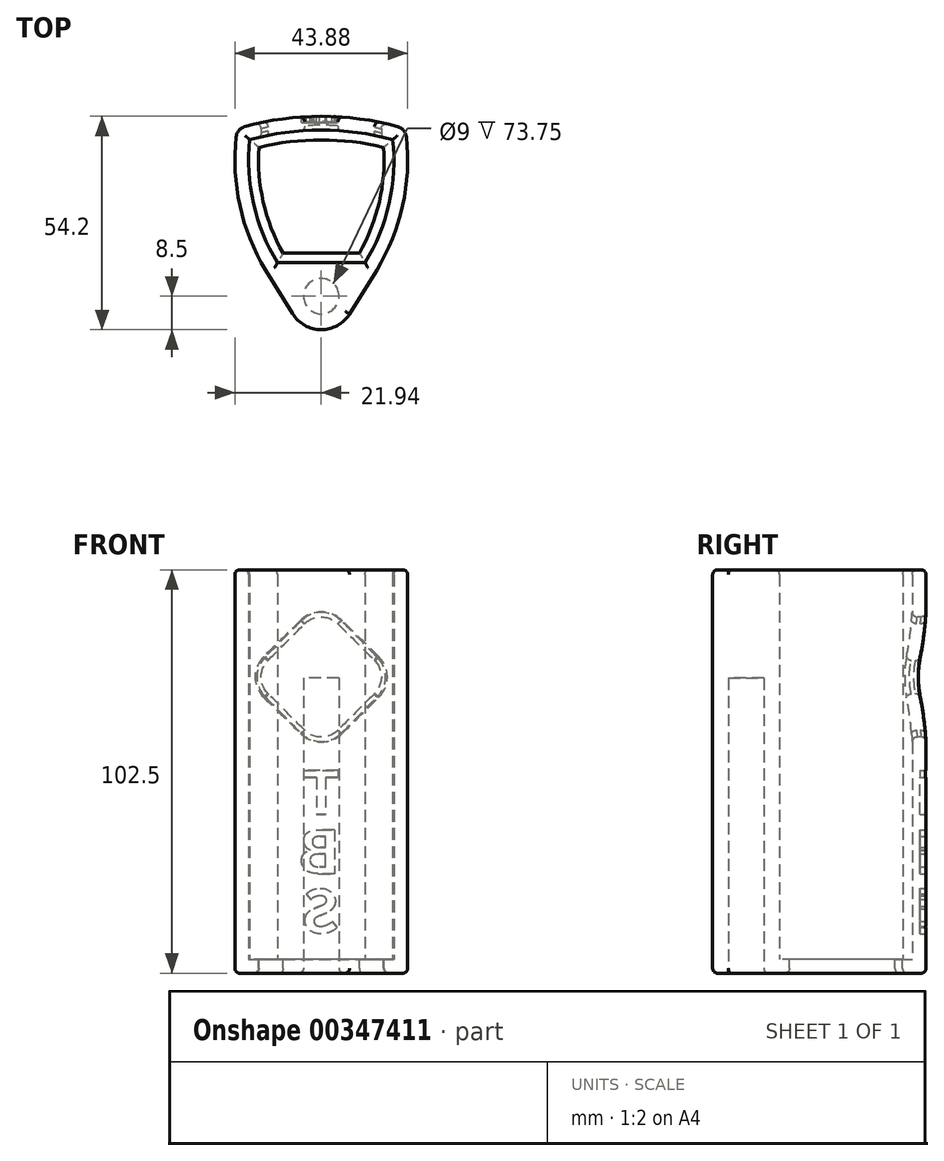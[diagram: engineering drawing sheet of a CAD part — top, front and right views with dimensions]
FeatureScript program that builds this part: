
annotation { "Feature Type Name" : "Feature", "Feature Type Description" : "" }
export const myFeature = defineFeature(function(context is Context, id is Id, definition is map)
    precondition{}
    {
        {
            var Q0;
            Q0=qCreatedBy(makeId("Top.planeOp"),FACE);
            var sketch = newSketch(context, id + "F0", { "sketchPlane" : qUnion([Q0])});
            skLineSegment(sketch, "E0", {"start": v(0, 0) * mm, "end": v(11.12, 0) * mm});
            skLineSegment(sketch, "E1", {"start": v(11.12, 0) * mm, "end": v(-11.12, 0) * mm});
            skArc(sketch, "E2", {"start": v(-18.16, 31.28) * mm, "mid": v(-17.22, 15.06) * mm, "end": v(-11.13, 0) * mm});
            skArc(sketch, "E3", {"start": v(11.13, 0) * mm, "mid": v(17.22, 15.06) * mm, "end": v(18.16, 31.28) * mm});
            skArc(sketch, "E4", {"start": v(18.16, 31.28) * mm, "mid": v(0, 33.7) * mm, "end": v(-18.16, 31.28) * mm});
            skArc(sketch, "E5.0", {"start": v(-21.34, 34) * mm, "mid": v(-20.88, 15.46) * mm, "end": v(-14.11, -1.82) * mm});
            skArc(sketch, "E5.1", {"start": v(21.34, 34) * mm, "mid": v(0, 37.2) * mm, "end": v(-21.34, 34) * mm});
            skArc(sketch, "E5.2", {"start": v(14.11, -1.82) * mm, "mid": v(20.88, 15.46) * mm, "end": v(21.34, 34) * mm});
            skCircle(sketch, "E6", {"center": v(0, -8.5) * mm, "radius": 4.5 * mm});
            skLineSegment(sketch, "E7", {"start": v(-14.11, -1.82) * mm, "end": v(-7.23, -12.97) * mm});
            skLineSegment(sketch, "E8", {"start": v(7.19, -13.03) * mm, "end": v(14.11, -1.82) * mm});
            skArc(sketch, "E9", {"start": v(-7.23, -12.97) * mm, "mid": v(-0.04, -17) * mm, "end": v(7.19, -13.03) * mm});
            skLineSegment(sketch, "E10", {"start": v(21.34, 34) * mm, "end": v(21.34, 39.15) * mm});
            skLineSegment(sketch, "E11", {"start": v(21.34, 39.15) * mm, "end": v(-21.34, 39.15) * mm});
            skLineSegment(sketch, "E12", {"start": v(-21.34, 39.15) * mm, "end": v(-21.34, 34) * mm});
            skSolve(sketch);
        }
        {
            var Q0;
            {var subQ3=sQuery(id+"F0.wireOp",EDGE,"E2");Q0=makeQuery(id+"F0.imprint","IMPRINT",FACE,{"disambiguationData":[TD([[makeQuery(id+"F0.imprint","IMPRINT",EDGE,{"derivedFrom":subQ3}),-1.0]])]});}
            var Q1;
            Q1=makeQuery(id+"F0.imprint","IMPRINT",FACE,{"disambiguationData":[TD([[makeQuery(id+"F0.imprint","IMPRINT",EDGE,{"derivedFrom":sQuery(id+"F0.wireOp",EDGE,"E6")}),1.0]])]});
            extrude(context, id + "F1", {"entities" : qUnion([Q0, Q1]), "depth" : 102.5 * mm});
        }
        {
            var Q0;
            {var subQ1=sQuery(id+"F0.wireOp",EDGE,"E2");Q0=makeQuery(id+"F0.imprint","IMPRINT",FACE,{"disambiguationData":[TD([[makeQuery(id+"F0.imprint","IMPRINT",EDGE,{"derivedFrom":subQ1}),1.0]])]});}
            extrude(context, id + "F2", {"entities" : qUnion([Q0]), "operationType" : NewBodyOperationType.ADD, "depth" : 3.5 * mm});
        }
        {
            var Q0;
            Q0=makeQuery(id+"F0.imprint","IMPRINT",FACE,{"disambiguationData":[TD([[makeQuery(id+"F0.imprint","IMPRINT",EDGE,{"derivedFrom":sQuery(id+"F0.wireOp",EDGE,"E6")}),1.0]])]});
            extrude(context, id + "F3", {"entities" : qUnion([Q0]), "operationType" : NewBodyOperationType.REMOVE, "depth" : 75 * mm});
        }
        {
            var Q0;
            Q0=makeQuery(id+"F0.imprint","IMPRINT",FACE,{"disambiguationData":[TD([[makeQuery(id+"F0.imprint","IMPRINT",EDGE,{"derivedFrom":sQuery(id+"F0.wireOp",EDGE,"E5.1")}),-1.0]])]});
            extrude(context, id + "F4", {"entities" : qUnion([Q0]), "operationType" : NewBodyOperationType.ADD, "depth" : 102.5 * mm});
        }
        {
            var Q0;
            Q0=makeQuery(id+"F4.opExtrude","SWEPT_FACE",FACE,{"disambiguationData":[OSD([sQuery(id+"F0.wireOp",EDGE,"E11")])]});
            var sketch = newSketch(context, id + "F5", { "sketchPlane" : qUnion([Q0])});
            skPoint(sketch, "E13.endSnap0", {"position": v(0, 0) * mm});
            skLineSegment(sketch, "E14", {"start": v(-17.75, 75.25) * mm, "end": v(0, 93) * mm});
            skLineSegment(sketch, "E15", {"start": v(17.75, 75.25) * mm, "end": v(0, 57.5) * mm});
            skLineSegment(sketch, "E16", {"start": v(0, 57.5) * mm, "end": v(-17.75, 75.25) * mm});
            skLineSegment(sketch, "E17", {"start": v(0, 93) * mm, "end": v(17.75, 75.25) * mm});
            skLineSegment(sketch, "E18", {"start": v(0, 0) * mm, "end": v(0, 57.5) * mm});
            skSolve(sketch);
        }
        {
            var Q0;
            Q0=makeQuery(id+"F5.imprint","IMPRINT",FACE,{"disambiguationData":[TD([[makeQuery(id+"F5.imprint","IMPRINT",EDGE,{"derivedFrom":sQuery(id+"F5.wireOp",EDGE,"E14")}),-1.0]])]});
            extrude(context, id + "F6", {"entities" : qUnion([Q0]), "operationType" : NewBodyOperationType.REMOVE, "oppositeDirection" : true, "depth" : 10 * mm});
        }
        {
            var Q0;
            Q0=makeQuery(id+"F6.boolean.opBoolean","COPY",EDGE,{"derivedFrom":makeQuery(id+"F6.opExtrude","SWEPT_EDGE",EDGE,{"disambiguationData":[OSD([sQuery(id+"F5.wireOp",EDGE,"E15"),sQuery(id+"F5.wireOp",EDGE,"E17")])]})});
            var Q1;
            Q1=makeQuery(id+"F6.boolean.opBoolean","COPY",EDGE,{"derivedFrom":makeQuery(id+"F6.opExtrude","SWEPT_EDGE",EDGE,{"disambiguationData":[OSD([sQuery(id+"F5.wireOp",EDGE,"E15"),sQuery(id+"F5.wireOp",EDGE,"E16")])]})});
            var Q2;
            Q2=makeQuery(id+"F6.boolean.opBoolean","COPY",EDGE,{"derivedFrom":makeQuery(id+"F6.opExtrude","SWEPT_EDGE",EDGE,{"disambiguationData":[OSD([sQuery(id+"F5.wireOp",EDGE,"E14"),sQuery(id+"F5.wireOp",EDGE,"E16")])]})});
            var Q3;
            Q3=makeQuery(id+"F6.boolean.opBoolean","COPY",EDGE,{"derivedFrom":makeQuery(id+"F6.opExtrude","SWEPT_EDGE",EDGE,{"disambiguationData":[OSD([sQuery(id+"F5.wireOp",EDGE,"E14"),sQuery(id+"F5.wireOp",EDGE,"E17")])]})});
            fillet(context, id + "F7", {"entities" : qUnion([Q0, Q1, Q2, Q3]), "radius" : 6 * mm, "tangentPropagation" : true, "allowEdgeOverflow" : false});
        }
        {
            var Q0;
            Q0=makeQuery(id+"F4.opExtrude","SWEPT_FACE",FACE,{"disambiguationData":[OSD([sQuery(id+"F0.wireOp",EDGE,"E11")])]});
            var sketch = newSketch(context, id + "F8", { "sketchPlane" : qUnion([Q0])});
            skText(sketch, "E19", { "text": "T\nB\nS", "fontName": "NotoSansCJKsc-Bold.otf"});
            skPoint(sketch, "E19.firstSnap0", {"position": v(-21.34, 51.25) * mm});
            const initialGuessF8  = {"E19": [-0.00469, 0.04038, 1, 0, 0.01087]};
            skSetInitialGuess(sketch, initialGuessF8);
            skSolve(sketch);
        }
        {
            var Q0;
            Q0=qSketchRegion(id+"F8",true);
            extrude(context, id + "F9", {"entities" : qUnion([Q0]), "operationType" : NewBodyOperationType.REMOVE, "oppositeDirection" : true, "depth" : 4 * mm});
        }
        {
            var Q0;
            Q0=makeQuery(id+"F0.imprint","IMPRINT",FACE,{"disambiguationData":[TD([[makeQuery(id+"F0.imprint","IMPRINT",EDGE,{"derivedFrom":sQuery(id+"F0.wireOp",EDGE,"E5.1")}),-1.0]])]});
            extrude(context, id + "F10", {"entities" : qUnion([Q0]), "operationType" : NewBodyOperationType.REMOVE, "depth" : 102.5 * mm});
        }
        {
            var Q0;
            Q0=makeQuery(id+"F9.boolean.opBoolean","COPY",FACE,{"derivedFrom":makeQuery(id+"F9.opExtrude","CAP_FACE",FACE,{"disambiguationData":[OSD([sQuery(id+"F8.wireOp",EDGE,"E19.sketch_text.stroke-0"),sQuery(id+"F8.wireOp",EDGE,"E19.sketch_text.stroke-1"),sQuery(id+"F8.wireOp",EDGE,"E19.sketch_text.stroke-2"),sQuery(id+"F8.wireOp",EDGE,"E19.sketch_text.stroke-3"),sQuery(id+"F8.wireOp",EDGE,"E19.sketch_text.stroke-4"),sQuery(id+"F8.wireOp",EDGE,"E19.sketch_text.stroke-5"),sQuery(id+"F8.wireOp",EDGE,"E19.sketch_text.stroke-6"),sQuery(id+"F8.wireOp",EDGE,"E19.sketch_text.stroke-7")])],"isStart":false})});
            var Q1;
            Q1=makeQuery(id+"F9.boolean.opBoolean","COPY",FACE,{"derivedFrom":makeQuery(id+"F9.opExtrude","CAP_FACE",FACE,{"disambiguationData":[OSD([sQuery(id+"F8.wireOp",EDGE,"E19.sketch_text.stroke-8"),sQuery(id+"F8.wireOp",EDGE,"E19.sketch_text.stroke-9"),sQuery(id+"F8.wireOp",EDGE,"E19.sketch_text.stroke-10"),sQuery(id+"F8.wireOp",EDGE,"E19.sketch_text.stroke-11"),sQuery(id+"F8.wireOp",EDGE,"E19.sketch_text.stroke-12"),sQuery(id+"F8.wireOp",EDGE,"E19.sketch_text.stroke-13"),sQuery(id+"F8.wireOp",EDGE,"E19.sketch_text.stroke-14"),sQuery(id+"F8.wireOp",EDGE,"E19.sketch_text.stroke-15"),sQuery(id+"F8.wireOp",EDGE,"E19.sketch_text.stroke-16"),sQuery(id+"F8.wireOp",EDGE,"E19.sketch_text.stroke-17"),sQuery(id+"F8.wireOp",EDGE,"E19.sketch_text.stroke-18"),sQuery(id+"F8.wireOp",EDGE,"E19.sketch_text.stroke-19"),sQuery(id+"F8.wireOp",EDGE,"E19.sketch_text.stroke-20"),sQuery(id+"F8.wireOp",EDGE,"E19.sketch_text.stroke-21"),sQuery(id+"F8.wireOp",EDGE,"E19.sketch_text.stroke-22"),sQuery(id+"F8.wireOp",EDGE,"E19.sketch_text.stroke-23"),sQuery(id+"F8.wireOp",EDGE,"E19.sketch_text.stroke-24"),sQuery(id+"F8.wireOp",EDGE,"E19.sketch_text.stroke-25")])],"isStart":false})});
            var Q2;
            Q2=makeQuery(id+"F9.boolean.opBoolean","COPY",FACE,{"derivedFrom":makeQuery(id+"F9.opExtrude","CAP_FACE",FACE,{"disambiguationData":[OSD([sQuery(id+"F8.wireOp",EDGE,"E19.sketch_text.stroke-26"),sQuery(id+"F8.wireOp",EDGE,"E19.sketch_text.stroke-27"),sQuery(id+"F8.wireOp",EDGE,"E19.sketch_text.stroke-28"),sQuery(id+"F8.wireOp",EDGE,"E19.sketch_text.stroke-29"),sQuery(id+"F8.wireOp",EDGE,"E19.sketch_text.stroke-30"),sQuery(id+"F8.wireOp",EDGE,"E19.sketch_text.stroke-31"),sQuery(id+"F8.wireOp",EDGE,"E19.sketch_text.stroke-32"),sQuery(id+"F8.wireOp",EDGE,"E19.sketch_text.stroke-33"),sQuery(id+"F8.wireOp",EDGE,"E19.sketch_text.stroke-34"),sQuery(id+"F8.wireOp",EDGE,"E19.sketch_text.stroke-35"),sQuery(id+"F8.wireOp",EDGE,"E19.sketch_text.stroke-36"),sQuery(id+"F8.wireOp",EDGE,"E19.sketch_text.stroke-37"),sQuery(id+"F8.wireOp",EDGE,"E19.sketch_text.stroke-38"),sQuery(id+"F8.wireOp",EDGE,"E19.sketch_text.stroke-39"),sQuery(id+"F8.wireOp",EDGE,"E19.sketch_text.stroke-40"),sQuery(id+"F8.wireOp",EDGE,"E19.sketch_text.stroke-41")])],"isStart":false})});
            extrude(context, id + "F11", {"entities" : qUnion([Q0, Q1, Q2]), "operationType" : NewBodyOperationType.ADD, "depth" : .5 * mm});
        }
        {
            var Q0;
            {var subQ0=sQuery(id+"F0.wireOp",EDGE,"E12");var subQ1=sQuery(id+"F0.wireOp",EDGE,"E5.1");var subQ2=sQuery(id+"F0.wireOp",EDGE,"E5.0");Q0=makeQuery(id+"F10.boolean.opBoolean","MERGE",EDGE,{"derivedFrom":[makeQuery(id+"F4.boolean.opBoolean","MERGE",EDGE,{"derivedFrom":[makeQuery(id+"F1.opExtrude","SWEPT_EDGE",EDGE,{"disambiguationData":[OSD([subQ2,subQ1,subQ0])]}),makeQuery(id+"F4.opExtrude","SWEPT_EDGE",EDGE,{"disambiguationData":[OSD([subQ2,subQ1,subQ0])]})]}),makeQuery(id+"F10.opExtrude","SWEPT_EDGE",EDGE,{"disambiguationData":[OSD([subQ2,subQ1,subQ0])]})]});}
            var Q1;
            {var subQ0=sQuery(id+"F0.wireOp",EDGE,"E10");var subQ1=sQuery(id+"F0.wireOp",EDGE,"E5.2");var subQ2=sQuery(id+"F0.wireOp",EDGE,"E5.1");Q1=makeQuery(id+"F10.boolean.opBoolean","MERGE",EDGE,{"derivedFrom":[makeQuery(id+"F4.boolean.opBoolean","MERGE",EDGE,{"derivedFrom":[makeQuery(id+"F1.opExtrude","SWEPT_EDGE",EDGE,{"disambiguationData":[OSD([subQ2,subQ1,subQ0])]}),makeQuery(id+"F4.opExtrude","SWEPT_EDGE",EDGE,{"disambiguationData":[OSD([subQ2,subQ1,subQ0])]})]}),makeQuery(id+"F10.opExtrude","SWEPT_EDGE",EDGE,{"disambiguationData":[OSD([subQ2,subQ1,subQ0])]})]});}
            fillet(context, id + "F12", {"entities" : qUnion([Q0, Q1]), "radius" : 3 * mm, "tangentPropagation" : true, "allowEdgeOverflow" : false});
        }
        {
            var Q0;
            Q0=makeQuery(id+"F2.opExtrude","CAP_FACE",FACE,{"disambiguationData":[OSD([sQuery(id+"F0.wireOp",EDGE,"E1"),sQuery(id+"F0.wireOp",EDGE,"E2"),sQuery(id+"F0.wireOp",EDGE,"E3"),sQuery(id+"F0.wireOp",EDGE,"E4")])],"isStart":false});
            var sketch = newSketch(context, id + "F13", { "sketchPlane" : qUnion([Q0])});
            skArc(sketch, "E20.0", {"start": v(9.7, 2.5) * mm, "mid": v(14.75, 15.45) * mm, "end": v(15.83, 29.3) * mm});
            skLineSegment(sketch, "E20.1", {"start": v(-9.7, 2.5) * mm, "end": v(9.7, 2.5) * mm});
            skArc(sketch, "E20.2", {"start": v(-15.83, 29.3) * mm, "mid": v(-14.75, 15.45) * mm, "end": v(-9.7, 2.5) * mm});
            skArc(sketch, "E20.3", {"start": v(15.83, 29.3) * mm, "mid": v(0, 31.2) * mm, "end": v(-15.83, 29.3) * mm});
            skSolve(sketch);
        }
        {
            var Q0;
            Q0=makeQuery(id+"F13.imprint","IMPRINT",FACE,{"disambiguationData":[TD([[makeQuery(id+"F13.imprint","IMPRINT",EDGE,{"derivedFrom":sQuery(id+"F13.wireOp",EDGE,"E20.0")}),1.0]])]});
            extrude(context, id + "F14", {"entities" : qUnion([Q0]), "operationType" : NewBodyOperationType.REMOVE, "oppositeDirection" : true, "depth" : 25 * mm});
        }
        {
            var Q0;
            {var subQ0=sQuery(id+"F0.wireOp",EDGE,"E5.1");var subQ1=sQuery(id+"F0.wireOp",EDGE,"E4");var subQ2=sQuery(id+"F0.wireOp",EDGE,"E3");var subQ3=sQuery(id+"F0.wireOp",EDGE,"E2");var subQ4=sQuery(id+"F0.wireOp",EDGE,"E1");Q0=makeQuery(id+"F4.boolean.opBoolean","MERGE",FACE,{"derivedFrom":[makeQuery(id+"F2.boolean.opBoolean","MERGE",FACE,{"derivedFrom":[makeQuery(id+"F1.opExtrude","CAP_FACE",FACE,{"disambiguationData":[OSD([subQ4,subQ3,subQ2,subQ1,sQuery(id+"F0.wireOp",EDGE,"E5.0"),subQ0,sQuery(id+"F0.wireOp",EDGE,"E5.2"),sQuery(id+"F0.wireOp",EDGE,"E7"),sQuery(id+"F0.wireOp",EDGE,"E8"),sQuery(id+"F0.wireOp",EDGE,"E9")])],"isStart":true}),makeQuery(id+"F2.opExtrude","CAP_FACE",FACE,{"disambiguationData":[OSD([subQ4,subQ3,subQ2,subQ1])],"isStart":true})]}),makeQuery(id+"F4.opExtrude","CAP_FACE",FACE,{"disambiguationData":[OSD([subQ0,sQuery(id+"F0.wireOp",EDGE,"E10"),sQuery(id+"F0.wireOp",EDGE,"E11"),sQuery(id+"F0.wireOp",EDGE,"E12")])],"isStart":true})]});}
            fillet(context, id + "F15", {"entities" : qUnion([Q0]), "radius" : 1.25 * mm, "tangentPropagation" : true, "allowEdgeOverflow" : false});
        }
        {
            var Q0;
            {var subQ0=sQuery(id+"F0.wireOp",EDGE,"E5.1");Q0=makeQuery(id+"F4.boolean.opBoolean","MERGE",FACE,{"derivedFrom":[makeQuery(id+"F1.opExtrude","CAP_FACE",FACE,{"disambiguationData":[OSD([sQuery(id+"F0.wireOp",EDGE,"E1"),sQuery(id+"F0.wireOp",EDGE,"E2"),sQuery(id+"F0.wireOp",EDGE,"E3"),sQuery(id+"F0.wireOp",EDGE,"E4"),sQuery(id+"F0.wireOp",EDGE,"E5.0"),subQ0,sQuery(id+"F0.wireOp",EDGE,"E5.2"),sQuery(id+"F0.wireOp",EDGE,"E7"),sQuery(id+"F0.wireOp",EDGE,"E8"),sQuery(id+"F0.wireOp",EDGE,"E9")])],"isStart":false}),makeQuery(id+"F4.opExtrude","CAP_FACE",FACE,{"disambiguationData":[OSD([subQ0,sQuery(id+"F0.wireOp",EDGE,"E10"),sQuery(id+"F0.wireOp",EDGE,"E11"),sQuery(id+"F0.wireOp",EDGE,"E12")])],"isStart":false})]});}
            fillet(context, id + "F16", {"entities" : qUnion([Q0]), "radius" : 1.25 * mm, "tangentPropagation" : true, "allowEdgeOverflow" : false});
        }
        {
            var Q0;
            Q0=makeQuery(id+"F10.boolean.opBoolean","INTERSECT",EDGE,{"derivedFrom":[makeQuery(id+"F7.opFillet","BLEND_FACE",FACE,{"disambiguationData":[OSD([sQuery(id+"F5.wireOp",EDGE,"E15"),sQuery(id+"F5.wireOp",EDGE,"E17")])]}),makeQuery(id+"F10.opExtrude","SWEPT_FACE",FACE,{"disambiguationData":[OSD([sQuery(id+"F0.wireOp",EDGE,"E5.1")])]})]});
            var Q1;
            Q1=makeQuery(id+"F7.opFillet","BLEND_EDGE",EDGE,{"blendedFrom":[makeQuery(id+"F6.boolean.opBoolean","COPY",EDGE,{"derivedFrom":makeQuery(id+"F6.opExtrude","SWEPT_EDGE",EDGE,{"disambiguationData":[OSD([sQuery(id+"F5.wireOp",EDGE,"E15"),sQuery(id+"F5.wireOp",EDGE,"E17")])]})}),makeQuery(id+"F1.opExtrude","SWEPT_FACE",FACE,{"disambiguationData":[OSD([sQuery(id+"F0.wireOp",EDGE,"E4")])]})],"blendedInto":[makeQuery(id+"F1.opExtrude","SWEPT_FACE",FACE,{"disambiguationData":[OSD([sQuery(id+"F0.wireOp",EDGE,"E4")])]})]});
            fillet(context, id + "F17", {"entities" : qUnion([Q0, Q1]), "radius" : 1.25 * mm, "tangentPropagation" : true, "allowEdgeOverflow" : false});
        }
    });
